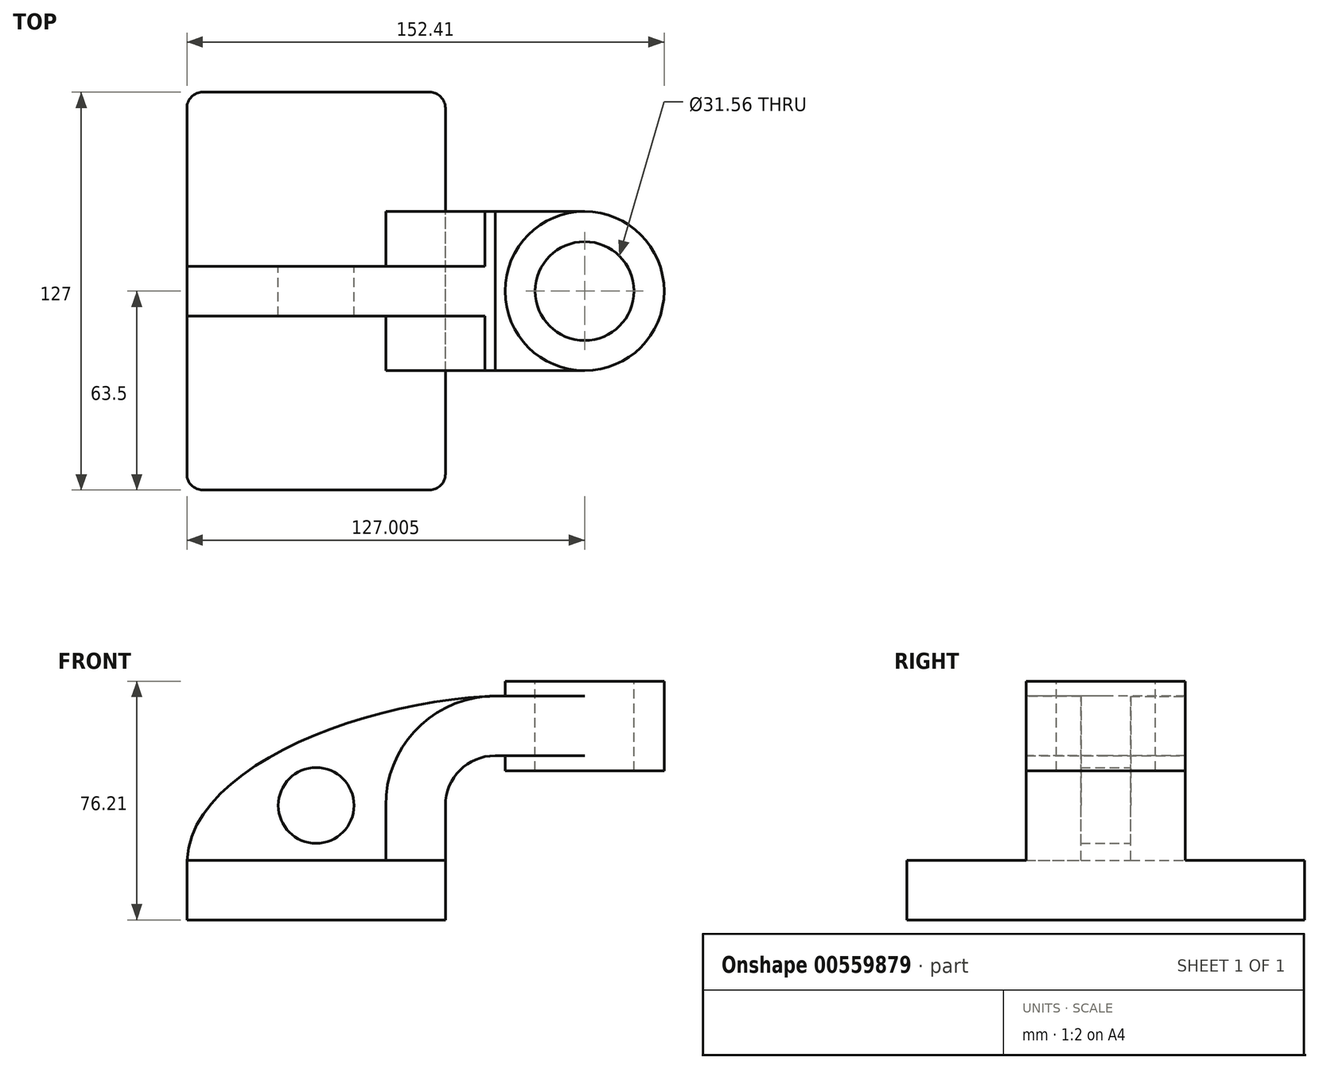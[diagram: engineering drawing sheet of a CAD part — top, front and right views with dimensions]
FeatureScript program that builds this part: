
annotation { "Feature Type Name" : "Feature", "Feature Type Description" : "" }
export const myFeature = defineFeature(function(context is Context, id is Id, definition is map)
    precondition{}
    {
        {
            var Q0;
            Q0=qCreatedBy(makeId("Front.planeOp"),FACE);
            var sketch = newSketch(context, id + "F0", { "sketchPlane" : qUnion([Q0])});
            skLineSegment(sketch, "E0.rect.bottom", {"start": v(-41.28, 9.52) * mm, "end": v(41.28, 9.52) * mm});
            skLineSegment(sketch, "E0.rect.top", {"start": v(-41.28, -9.52) * mm, "end": v(41.28, -9.52) * mm});
            skLineSegment(sketch, "E0.rect.left", {"start": v(-41.28, 9.52) * mm, "end": v(-41.28, -9.52) * mm});
            skLineSegment(sketch, "E0.rect.right", {"start": v(41.28, 9.52) * mm, "end": v(41.28, -9.52) * mm});
            skPoint(sketch, "E0.rect.middle", {"position": v(0, 0) * mm});
            skLineSegment(sketch, "E1", {"start": v(41.28, 9.52) * mm, "end": v(41.28, 27) * mm});
            skArc(sketch, "E2", {"start": v(41.28, 27) * mm, "mid": v(45.92, 38.23) * mm, "end": v(57.15, 42.88) * mm});
            skLineSegment(sketch, "E3", {"start": v(57.15, 42.88) * mm, "end": v(85.72, 42.88) * mm});
            skLineSegment(sketch, "E4.rect.bottom", {"start": v(60.32, 38.1) * mm, "end": v(111.12, 38.1) * mm});
            skLineSegment(sketch, "E4.rect.top", {"start": v(60.32, 66.68) * mm, "end": v(111.12, 66.68) * mm});
            skLineSegment(sketch, "E4.rect.left", {"start": v(60.32, 38.1) * mm, "end": v(60.32, 66.68) * mm});
            skLineSegment(sketch, "E4.rect.right", {"start": v(111.13, 38.1) * mm, "end": v(111.12, 66.68) * mm});
            skPoint(sketch, "E4.rect.middle", {"position": v(85.72, 52.39) * mm});
            skLineSegment(sketch, "E5.0", {"start": v(57.15, 61.93) * mm, "end": v(85.72, 61.93) * mm});
            skArc(sketch, "E5.1", {"start": v(22.23, 27) * mm, "mid": v(32.45, 51.7) * mm, "end": v(57.15, 61.93) * mm});
            skLineSegment(sketch, "E5.2", {"start": v(22.23, 9.52) * mm, "end": v(22.23, 27) * mm});
            skLineSegment(sketch, "E6", {"start": v(85.72, 38.1) * mm, "end": v(85.72, 66.68) * mm});
            skFitSpline(sketch, "E7", {"points": [v(-41.28, 9.53) * mm, v(57.15, 61.93) * mm], "startDerivative": vector(5.2, 92.34) * mm, "endDerivative": vector(120.92, 4.22) * mm});
            skCircle(sketch, "E8", {"center": v(0, 27) * mm, "radius": 12.1 * mm});
            skSolve(sketch);
        }
        {
            var Q0;
            Q0=makeQuery(id+"F0.imprint","IMPRINT",FACE,{"disambiguationData":[TD([[makeQuery(id+"F0.imprint","IMPRINT",EDGE,{"derivedFrom":sQuery(id+"F0.wireOp",EDGE,"E0.rect.top")}),1.0]])]});
            extrude(context, id + "F1", {"entities" : qUnion([Q0]), "endBound" : BoundingType.SYMMETRIC, "depth" : 127 * mm});
        }
        {
            var Q0;
            {var subQ9=sQuery(id+"F0.wireOp",EDGE,"E1");Q0=makeQuery(id+"F0.imprint","IMPRINT",FACE,{"disambiguationData":[TD([[makeQuery(id+"F0.imprint","IMPRINT",EDGE,{"derivedFrom":subQ9}),1.0]])]});}
            var Q1;
            {var subQ0=sQuery(id+"F0.wireOp",EDGE,"E6");var subQ1=sQuery(id+"F0.wireOp",EDGE,"E3");var subQ2=makeQuery(id+"F0.imprint","INTERSECT",VERTEX,{"derivedFrom":[subQ1,subQ0]});Q1=makeQuery(id+"F0.imprint","IMPRINT",FACE,{"disambiguationData":[TD([[makeQuery(id+"F0.imprint","IMPRINT",EDGE,{"disambiguationData":[TD([[subQ2,1.0]])],"derivedFrom":subQ1}),1.0]])]});}
            extrude(context, id + "F2", {"entities" : qUnion([Q0, Q1]), "operationType" : NewBodyOperationType.ADD, "endBound" : BoundingType.SYMMETRIC, "depth" : 50.8 * mm});
        }
        {
            var Q0;
            {var subQ3=sQuery(id+"F0.wireOp",EDGE,"E5.2");Q0=makeQuery(id+"F0.imprint","IMPRINT",FACE,{"disambiguationData":[TD([[makeQuery(id+"F0.imprint","IMPRINT",EDGE,{"derivedFrom":subQ3}),1.0]])]});}
            extrude(context, id + "F3", {"entities" : qUnion([Q0]), "operationType" : NewBodyOperationType.ADD, "endBound" : BoundingType.SYMMETRIC, "depth" : 15.88 * mm, "offsetDistance" : 25.4 * mm});
        }
        {
            var Q0;
            {var subQ5=sQuery(id+"F0.wireOp",EDGE,"E4.rect.right");Q0=makeQuery(id+"F0.imprint","IMPRINT",FACE,{"disambiguationData":[TD([[makeQuery(id+"F0.imprint","IMPRINT",EDGE,{"derivedFrom":subQ5}),1.0]])]});}
            var Q1;
            Q1=sQuery(id+"F0.wireOp",EDGE,"E6");
            revolve(context, id + "F4", {"operationType" : NewBodyOperationType.ADD, "entities" : qUnion([Q0]), "axis" : qUnion([Q1]), "revolveType" : RevolveType.FULL});
        }
        {
            var Q0;
            Q0=makeQuery(id+"F1.opExtrude","CAP_EDGE",EDGE,{"disambiguationData":[OSD([sQuery(id+"F0.wireOp",EDGE,"E0.rect.right")])],"isStart":false});
            var Q1;
            Q1=makeQuery(id+"F1.opExtrude","CAP_EDGE",EDGE,{"disambiguationData":[OSD([sQuery(id+"F0.wireOp",EDGE,"E0.rect.left")])],"isStart":false});
            var Q2;
            Q2=makeQuery(id+"F1.opExtrude","CAP_EDGE",EDGE,{"disambiguationData":[OSD([sQuery(id+"F0.wireOp",EDGE,"E0.rect.right")])],"isStart":true});
            var Q3;
            Q3=makeQuery(id+"F1.opExtrude","CAP_EDGE",EDGE,{"disambiguationData":[OSD([sQuery(id+"F0.wireOp",EDGE,"E0.rect.left")])],"isStart":true});
            fillet(context, id + "F5", {"entities" : qUnion([Q0, Q1, Q2, Q3]), "radius" : 5.08 * mm, "tangentPropagation" : true, "allowEdgeOverflow" : false});
        }
        {
            var Q0;
            Q0=makeQuery(id+"F4.opRevolve","SWEPT_FACE",FACE,{"disambiguationData":[OSD([sQuery(id+"F0.wireOp",EDGE,"E4.rect.top")])]});
            var sketch = newSketch(context, id + "F6", { "sketchPlane" : qUnion([Q0])});
            skCircle(sketch, "E9", {"center": v(85.72, 0) * mm, "radius": 15.78 * mm});
            skSolve(sketch);
        }
        {
            var Q0;
            Q0 = qSketchRegion(id + "F6", true);
            extrude(context, id + "F7", {"entities" : qUnion([Q0]), "operationType" : NewBodyOperationType.REMOVE, "endBound" : BoundingType.THROUGH_ALL, "oppositeDirection" : true, "depth" : 25.4 * mm, "offsetDistance" : 25.4 * mm});
        }
    });
